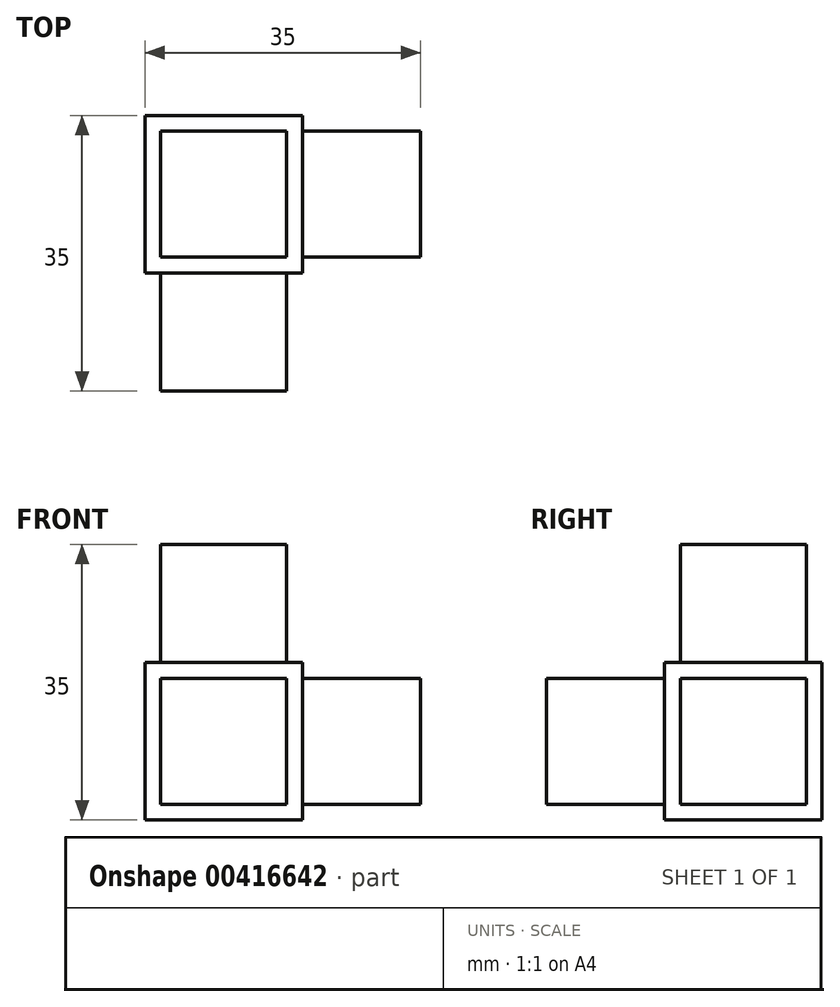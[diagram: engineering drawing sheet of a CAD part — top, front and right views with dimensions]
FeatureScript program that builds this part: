
annotation { "Feature Type Name" : "Feature", "Feature Type Description" : "" }
export const myFeature = defineFeature(function(context is Context, id is Id, definition is map)
    precondition{}
    {
        {
            var Q0;
            Q0=qCreatedBy(makeId("Front.planeOp"),FACE);
            var sketch = newSketch(context, id + "F0", { "sketchPlane" : qUnion([Q0])});
            skLineSegment(sketch, "E0.bottom", {"start": v(0, 0) * mm, "end": v(20, 0) * mm});
            skLineSegment(sketch, "E0.top", {"start": v(0, -20) * mm, "end": v(20, -20) * mm});
            skLineSegment(sketch, "E0.left", {"start": v(0, 0) * mm, "end": v(0, -20) * mm});
            skLineSegment(sketch, "E0.right", {"start": v(20, 0) * mm, "end": v(20, -20) * mm});
            skSolve(sketch);
        }
        {
            var Q0;
            Q0=qSketchRegion(id+"F0",true);
            extrude(context, id + "F1", {"entities" : qUnion([Q0]), "depth" : 20 * mm});
        }
        {
            var Q0;
            Q0=makeQuery(id+"F1.opExtrude","CAP_FACE",FACE,{"disambiguationData":[OSD([sQuery(id+"F0.wireOp",EDGE,"E0.bottom"),sQuery(id+"F0.wireOp",EDGE,"E0.top"),sQuery(id+"F0.wireOp",EDGE,"E0.left"),sQuery(id+"F0.wireOp",EDGE,"E0.right")])],"isStart":false});
            var sketch = newSketch(context, id + "F2", { "sketchPlane" : qUnion([Q0])});
            skLineSegment(sketch, "E1.bottom", {"start": v(18, -2) * mm, "end": v(2, -2) * mm});
            skLineSegment(sketch, "E1.top", {"start": v(18, -18) * mm, "end": v(2, -18) * mm});
            skLineSegment(sketch, "E1.left", {"start": v(18, -2) * mm, "end": v(18, -18) * mm});
            skLineSegment(sketch, "E1.right", {"start": v(2, -2) * mm, "end": v(2, -18) * mm});
            skSolve(sketch);
        }
        {
            var Q0;
            Q0=qSketchRegion(id+"F2",true);
            extrude(context, id + "F3", {"entities" : qUnion([Q0]), "operationType" : NewBodyOperationType.ADD, "depth" : 15 * mm});
        }
        {
            var Q0;
            Q0=makeQuery(id+"F1.opExtrude","SWEPT_FACE",FACE,{"disambiguationData":[OSD([sQuery(id+"F0.wireOp",EDGE,"E0.right")])]});
            var sketch = newSketch(context, id + "F4", { "sketchPlane" : qUnion([Q0])});
            skLineSegment(sketch, "E2.bottom", {"start": v(-2, -2) * mm, "end": v(-18, -2) * mm});
            skLineSegment(sketch, "E2.top", {"start": v(-2, -18) * mm, "end": v(-18, -18) * mm});
            skLineSegment(sketch, "E2.left", {"start": v(-2, -2) * mm, "end": v(-2, -18) * mm});
            skLineSegment(sketch, "E2.right", {"start": v(-18, -2) * mm, "end": v(-18, -18) * mm});
            skSolve(sketch);
        }
        {
            var Q0;
            Q0=qSketchRegion(id+"F4",true);
            extrude(context, id + "F5", {"entities" : qUnion([Q0]), "operationType" : NewBodyOperationType.ADD, "depth" : 15 * mm});
        }
        {
            var Q0;
            Q0=makeQuery(id+"F1.opExtrude","SWEPT_FACE",FACE,{"disambiguationData":[OSD([sQuery(id+"F0.wireOp",EDGE,"E0.bottom")])]});
            var sketch = newSketch(context, id + "F6", { "sketchPlane" : qUnion([Q0])});
            skLineSegment(sketch, "E3.bottom", {"start": v(18, -2) * mm, "end": v(2, -2) * mm});
            skLineSegment(sketch, "E3.top", {"start": v(18, -18) * mm, "end": v(2, -18) * mm});
            skLineSegment(sketch, "E3.left", {"start": v(18, -2) * mm, "end": v(18, -18) * mm});
            skLineSegment(sketch, "E3.right", {"start": v(2, -2) * mm, "end": v(2, -18) * mm});
            skSolve(sketch);
        }
        {
            var Q0;
            Q0=makeQuery(id+"F6.imprint","IMPRINT",FACE,{"disambiguationData":[TD([[makeQuery(id+"F6.imprint","IMPRINT",EDGE,{"derivedFrom":sQuery(id+"F6.wireOp",EDGE,"E3.bottom")}),1.0]])]});
            extrude(context, id + "F7", {"entities" : qUnion([Q0]), "operationType" : NewBodyOperationType.ADD, "depth" : 15 * mm});
        }
    });
